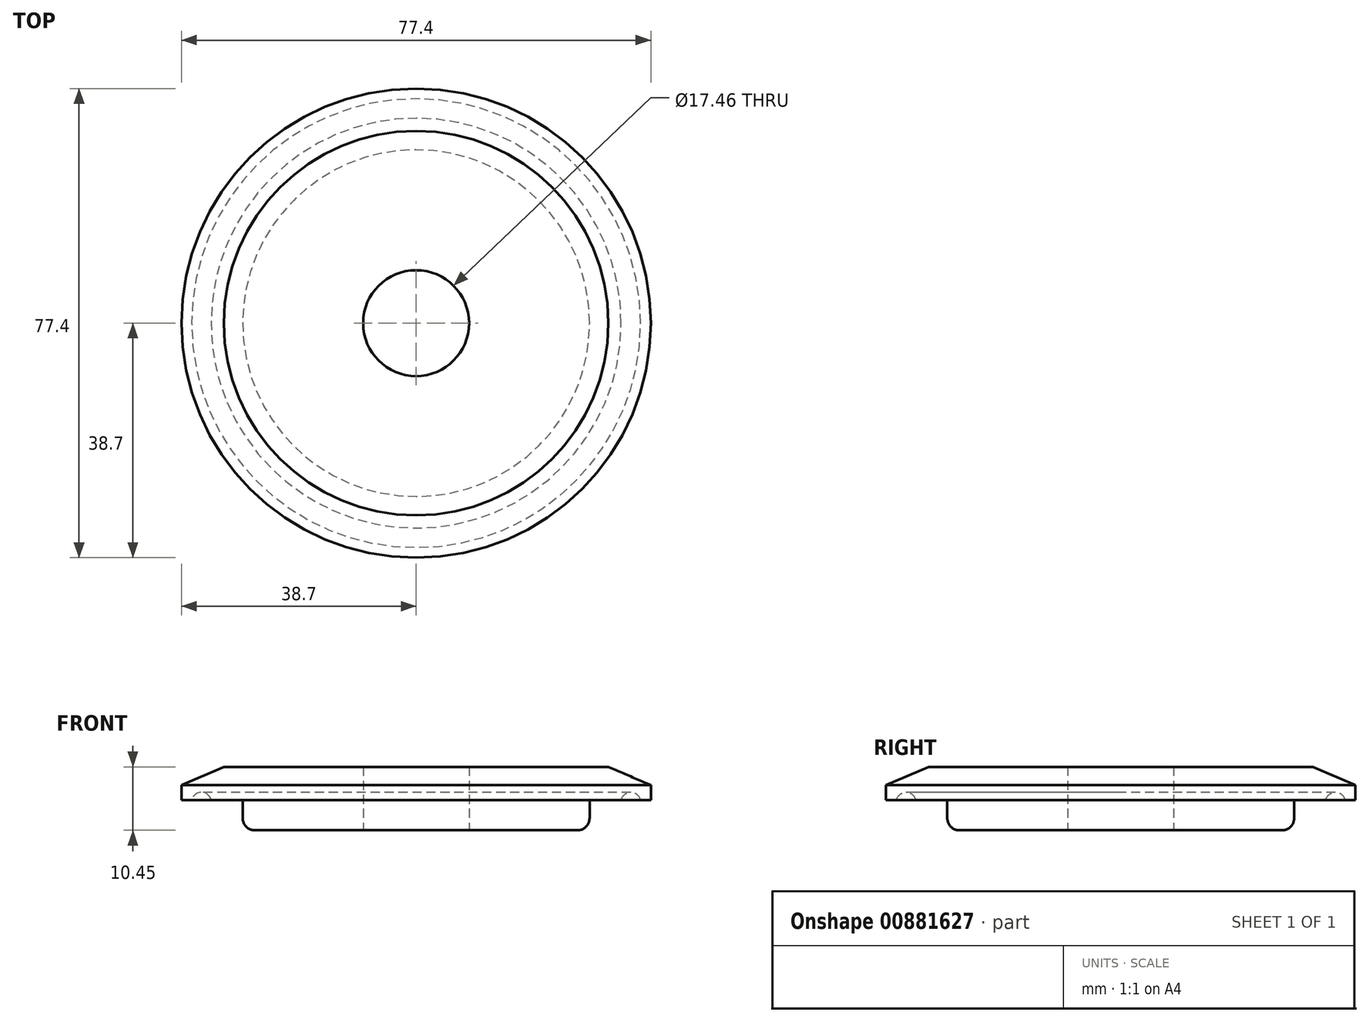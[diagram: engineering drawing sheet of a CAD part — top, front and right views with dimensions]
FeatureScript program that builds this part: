
annotation { "Feature Type Name" : "Feature", "Feature Type Description" : "" }
export const myFeature = defineFeature(function(context is Context, id is Id, definition is map)
    precondition{}
    {
        {
            var Q0;
            Q0=qCreatedBy(makeId("Top.planeOp"),FACE);
            var sketch = newSketch(context, id + "F0", { "sketchPlane" : qUnion([Q0])});
            skCircle(sketch, "E0", {"center": v(0, 0) * mm, "radius": 38.7 * mm});
            skSolve(sketch);
        }
        {
            var Q0;
            Q0 = qSketchRegion(id + "F0", true);
            extrude(context, id + "F1", {"entities" : qUnion([Q0]), "depth" : 5.45 * mm, "offsetDistance" : 25 * mm});
        }
        {
            var Q0;
            Q0=makeQuery(id+"F1.opExtrude","CAP_FACE",FACE,{"disambiguationData":[OSD([sQuery(id+"F0.wireOp",EDGE,"E0")])],"isStart":true});
            var sketch = newSketch(context, id + "F2", { "sketchPlane" : qUnion([Q0])});
            skCircle(sketch, "E1", {"center": v(0, 0) * mm, "radius": 28.6 * mm});
            skSolve(sketch);
        }
        {
            var Q0;
            Q0=makeQuery(id+"F2.imprint","IMPRINT",FACE,{"disambiguationData":[TD([[makeQuery(id+"F2.imprint","IMPRINT",EDGE,{"derivedFrom":sQuery(id+"F2.wireOp",EDGE,"E1")}),1.0]])]});
            extrude(context, id + "F3", {"entities" : qUnion([Q0]), "operationType" : NewBodyOperationType.ADD, "depth" : 5 * mm, "offsetDistance" : 25 * mm});
        }
        {
            var Q0;
            Q0=makeQuery(id+"F1.opExtrude","CAP_EDGE",EDGE,{"disambiguationData":[OSD([sQuery(id+"F0.wireOp",EDGE,"E0")])],"isStart":false});
            chamfer(context, id + "F4", {"entities" : qUnion([Q0]), "chamferType" : ChamferType.TWO_OFFSETS, "width1" : 7 * mm, "oppositeDirection" : false, "width2" : 3 * mm, "tangentPropagation" : true});
        }
        {
            var Q0;
            Q0=makeQuery(id+"F3.opExtrude","CAP_EDGE",EDGE,{"disambiguationData":[OSD([sQuery(id+"F2.wireOp",EDGE,"E1")])],"isStart":false});
            fillet(context, id + "F5", {"entities" : qUnion([Q0]), "radius" : 2 * mm, "tangentPropagation" : true, "allowEdgeOverflow" : false});
        }
        {
            var Q0;
            Q0=makeQuery(id+"F1.opExtrude","CAP_FACE",FACE,{"disambiguationData":[OSD([sQuery(id+"F0.wireOp",EDGE,"E0")])],"isStart":true});
            var sketch = newSketch(context, id + "F6", { "sketchPlane" : qUnion([Q0])});
            skCircle(sketch, "E2", {"center": v(0, 0) * mm, "radius": 35.2 * mm, "construction": true});
            skSolve(sketch);
        }
        {
            var Q0;
            Q0=makeQuery(id+"F3.opExtrude","CAP_FACE",FACE,{"disambiguationData":[OSD([sQuery(id+"F2.wireOp",EDGE,"E1")])],"isStart":false});
            var sketch = newSketch(context, id + "F7", { "sketchPlane" : qUnion([Q0])});
            skLineSegment(sketch, "E3", {"start": v(0, 0) * mm, "end": v(0, 26.6) * mm, "construction": true});
            skSolve(sketch);
        }
        {
            var Q0;
            Q0=sQuery(id+"F7.wireOp",VERTEX,"E3.end");
            var Q1;
            Q1=sQuery(id+"F7.wireOp",VERTEX,"E3.start");
            var Q2;
            Q2=sQuery(id+"F6.wireOp",VERTEX,"E2.center");
            cPlane(context, id + "F8", {"entities" : qUnion([Q0, Q1, Q2]), "cplaneType" : CPlaneType.THREE_POINT, "offset" : 25 * mm, "width" : 150 * mm, "height" : 150 * mm});
        }
        {
            var Q0;
            Q0=qCreatedBy(id+"F8.planeOp",FACE);
            var sketch = newSketch(context, id + "F9", { "sketchPlane" : qUnion([Q0])});
            skArc(sketch, "E4", {"start": v(37, 0) * mm, "mid": v(35.4, 1.25) * mm, "end": v(33.8, 0) * mm});
            skLineSegment(sketch, "E5", {"start": v(33.8, 0) * mm, "end": v(37, 0) * mm});
            skSolve(sketch);
        }
        {
            var Q0;
            Q0=qCreatedBy(makeId("Front.planeOp"),FACE);
            var sketch = newSketch(context, id + "F10", { "sketchPlane" : qUnion([Q0])});
            skLineSegment(sketch, "E6", {"start": v(0, 15.33) * mm, "end": v(0, 0) * mm, "construction": true});
            skSolve(sketch);
        }
        {
            var Q0;
            Q0 = qSketchRegion(id + "F9", true);
            var Q1;
            Q1=sQuery(id+"F10.wireOp",EDGE,"E6");
            revolve(context, id + "F11", {"operationType" : NewBodyOperationType.REMOVE, "surfaceOperationType" : NewSurfaceOperationType.NEW, "entities" : qUnion([Q0]), "axis" : qUnion([Q1]), "revolveType" : RevolveType.FULL, "oppositeDirection" : true});
        }
        {
            var Q0;
            Q0=sQuery(id+"F7.wireOp",VERTEX,"E3.start");
            var Q1;
            Q1=makeQuery(id+"F1.opExtrude","SWEPT_BODY",BODY,{"disambiguationData":[OSD([sQuery(id+"F0.wireOp",EDGE,"E0")])]});
            hole(context, id + "F12", {"style" : HoleStyle.SIMPLE, "endStyle" : HoleEndStyle.THROUGH, "standardTappedOrClearance" : lookupTablePath({ "standard" : "ANSI", "engagement" : "75%", "pitch" : "16 tpi", "size" : "3/4", "type" : "Tapped" }), "standardBlindInLast" : lookupTablePath({ "standard" : "ANSI", "engagement" : "75%", "pitch" : "16 tpi", "size" : "3/4", "type" : "Tapped" }), "holeDiameter" : 17.46 * mm, "majorDiameter" : 19.05 * mm, "showTappedDepth" : true, "isTappedThrough" : true, "tappedDepth" : 12 * mm, "tapClearance" : 3, "locations" : qUnion([Q0]), "scope" : qUnion([Q1])});
        }
    });
